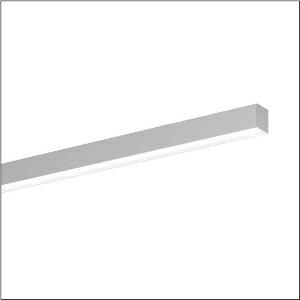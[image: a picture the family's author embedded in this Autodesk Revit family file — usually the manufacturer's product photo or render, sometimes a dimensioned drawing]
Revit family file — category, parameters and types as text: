
# Revit family: silica_r__21_51mx20dc35sb_d3c3
name_source: partatom
category: Lighting Fixtures
units: mm (PartAtom-declared; Revit-internal decimal feet)

## family parameters
Cut with Voids When Loaded = No
Host = Face
Light Source = No
Part Type = Normal
Room Calculation Point = No
Round Connector Dimension = Use Diameter
Shared = No

## types (1)
- --- (1 x LED, 6000 lm, 42.6 W, 3000K)
    Apparent Load = 43 VA
    CIE Flux Codes = 48 79 96 100 100
    Color Rendering = 80
    Color Temperature = 3000K
    Default Elevation = 1800 mm
    Description = Silica® 21, office luminaire, primary optical cover: cover, of PMMA, opal, light emission: direct distribution, primary light characteristic: symmetric, installation type: surface-mounted, LED, rated luminous flux: 6.000lm, luminous efficacy: 141lm/W, light colour: 830, colour temperature: 3000K, with terminal, 3+2-pole, max. 2.5mm², mains connection: 220..240V, AC, 50/60Hz, rated input power: 42.6W, luminaire housing, of aluminium, metallic grey (RAL 9006), length: 3.004mm, width: 53mm, height: 53mm, protection rating (complete): IP20, insulation class (complete): insulation class I (protective earthing), certification: CE, permissible operating ambient temperature: 0..+35°C, standard: EN 50419, packaging unit: 1 piece
    Height = 0 mm  [stored 0 ft]
    Lamp = 1 x LED
    Lamp Light Flux = 6000 lm
    Lamp Power = 42.6 W
    Lamp count = 1
    Length = 3004 mm
    Luminous efficacy = 141 lm/W
    Manufacturer = Siteco
    ModVariant = No
    Model = 51MX20DC35SB
    Mounting Place = Ceiling
    Mounting Type = Recessed
    Number of Poles = 1
    OnlyDefault = Yes
    Power Factor = 1
    Product Name = Silica® 21
    Product group = office luminaire | ceiling recessed
    ProductGroupID = 401
    Protection Class = Protection class I
    Protection Degree = IP 20
    RLX_Detail_Level = 1
    RLX_Emergency_Light_Flux = 0 lm
    RLX_Emergency_Type = 0
    RLX_Emergency_Type_DB = No
    RlxData = <blob elided: 26501 chars, md5=5de1e3a5>
    Socket = socket
    Standby Power = 0 W
    System Light Flux = 6000 lm
    System Power = 43 W
    Type Comments = factory setting: luminous flux: 100 % | dim-lin: 254 | 233 mA
    Type Image = l_1297768.jpg
    URL = http://relux.com
    VarID = @adj_047837
    Voltage = 0 V
    Weight = 0.00 kg
    Width = 53 mm

note: [stored X ft] marks values corroborated as IEEE doubles in the binary element streams (Revit-internal decimal feet)

## geometry (parser evidence)
native form markers: Blend x4, Sweep x9
no freeform markers — native parametric forms only
